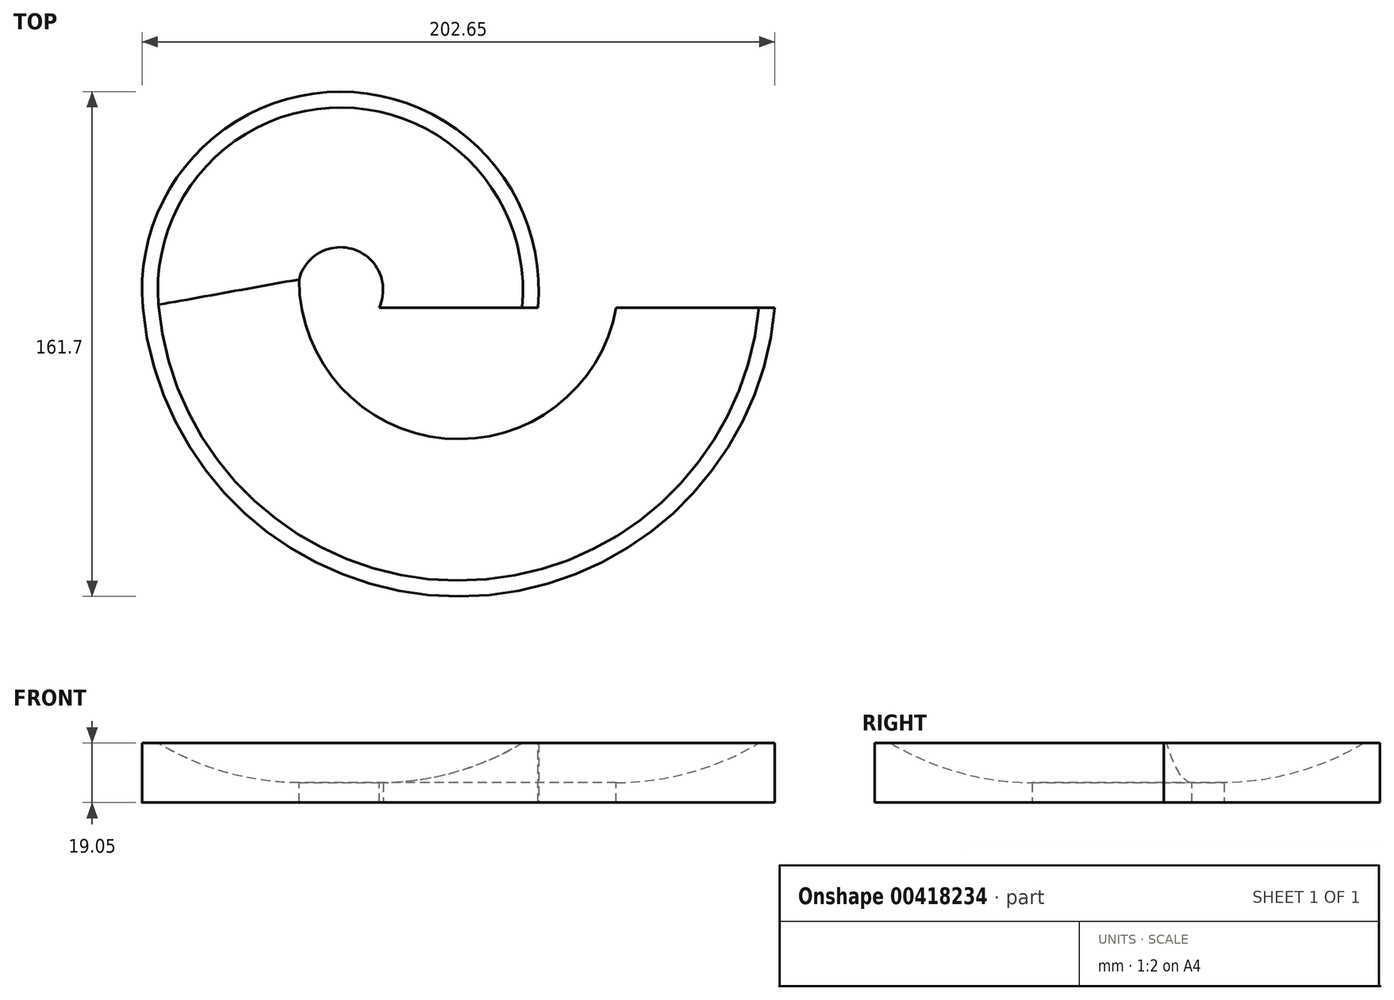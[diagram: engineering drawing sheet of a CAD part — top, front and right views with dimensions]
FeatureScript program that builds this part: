
annotation { "Feature Type Name" : "Feature", "Feature Type Description" : "" }
export const myFeature = defineFeature(function(context is Context, id is Id, definition is map)
    precondition{}
    {
        {
            var Q0;
            Q0=qCreatedBy(makeId("Front.planeOp"),FACE);
            var sketch = newSketch(context, id + "F0", { "sketchPlane" : qUnion([Q0])});
            skLineSegment(sketch, "E0", {"start": v(0, 0) * mm, "end": v(0, 19.05) * mm});
            skLineSegment(sketch, "E1", {"start": v(0, 0) * mm, "end": v(-50.8, 0) * mm});
            skLineSegment(sketch, "E2", {"start": v(-50.8, 0) * mm, "end": v(-50.8, 6.35) * mm});
            skLineSegment(sketch, "E3", {"start": v(0, 19.05) * mm, "end": v(-5.08, 19.05) * mm});
            skArc(sketch, "E4", {"start": v(-50.8, 6.35) * mm, "mid": v(-27.1, 9.65) * mm, "end": v(-5.08, 19.05) * mm});
            skFitSpline(sketch, "E5", {"points": [v(-68.1, 48.08) * mm, v(-43.3, 31.55) * mm, v(-43.91, 55.54) * mm, v(20.58, 73.07) * mm, v(33.48, 34.98) * mm, v(43.35, 71.06) * mm, v(-25.37, 96.25) * mm, v(-75.56, 81.13) * mm, v(-68.1, 48.08) * mm]});
            skSolve(sketch);
        }
        {
            var Q0;
            Q0=qCreatedBy(makeId("Top.planeOp"),FACE);
            var sketch = newSketch(context, id + "F1", { "sketchPlane" : qUnion([Q0])});
            skLineSegment(sketch, "E6", {"start": v(0, 0) * mm, "end": v(0, -101.6) * mm, "construction": true});
            skLineSegment(sketch, "E7", {"start": v(-444.5, -101.6) * mm, "end": v(-444.5, 101.6) * mm, "construction": true});
            skLineSegment(sketch, "E8", {"start": v(-444.5, 101.6) * mm, "end": v(0, 101.6) * mm, "construction": true});
            skLineSegment(sketch, "E9", {"start": v(0, 101.6) * mm, "end": v(0, 0) * mm, "construction": true});
            skArc(sketch, "E10", {"start": v(-202.4, 0) * mm, "mid": v(-101.2, -92.55) * mm, "end": v(0, 0) * mm});
            skPoint(sketch, "E10.startSnap0", {"position": v(-202.4, -101.6) * mm});
            skArc(sketch, "E11", {"start": v(-75.9, 0) * mm, "mid": v(-139.15, 69.15) * mm, "end": v(-202.4, 0) * mm});
            skSolve(sketch);
        }
        {
            var Q0;
            Q0=makeQuery(id+"F0.imprint","IMPRINT",FACE,{"disambiguationData":[TD([[makeQuery(id+"F0.imprint","IMPRINT",EDGE,{"derivedFrom":sQuery(id+"F0.wireOp",EDGE,"E0")}),1.0]])]});
            var Q1;
            Q1=sQuery(id+"F1.wireOp",EDGE,"E10");
            var Q2;
            Q2=sQuery(id+"F1.wireOp",EDGE,"E11");
            sweep(context, id + "F2", {"profiles" : qUnion([Q0]), "path" : qUnion([Q1, Q2])});
        }
    });
